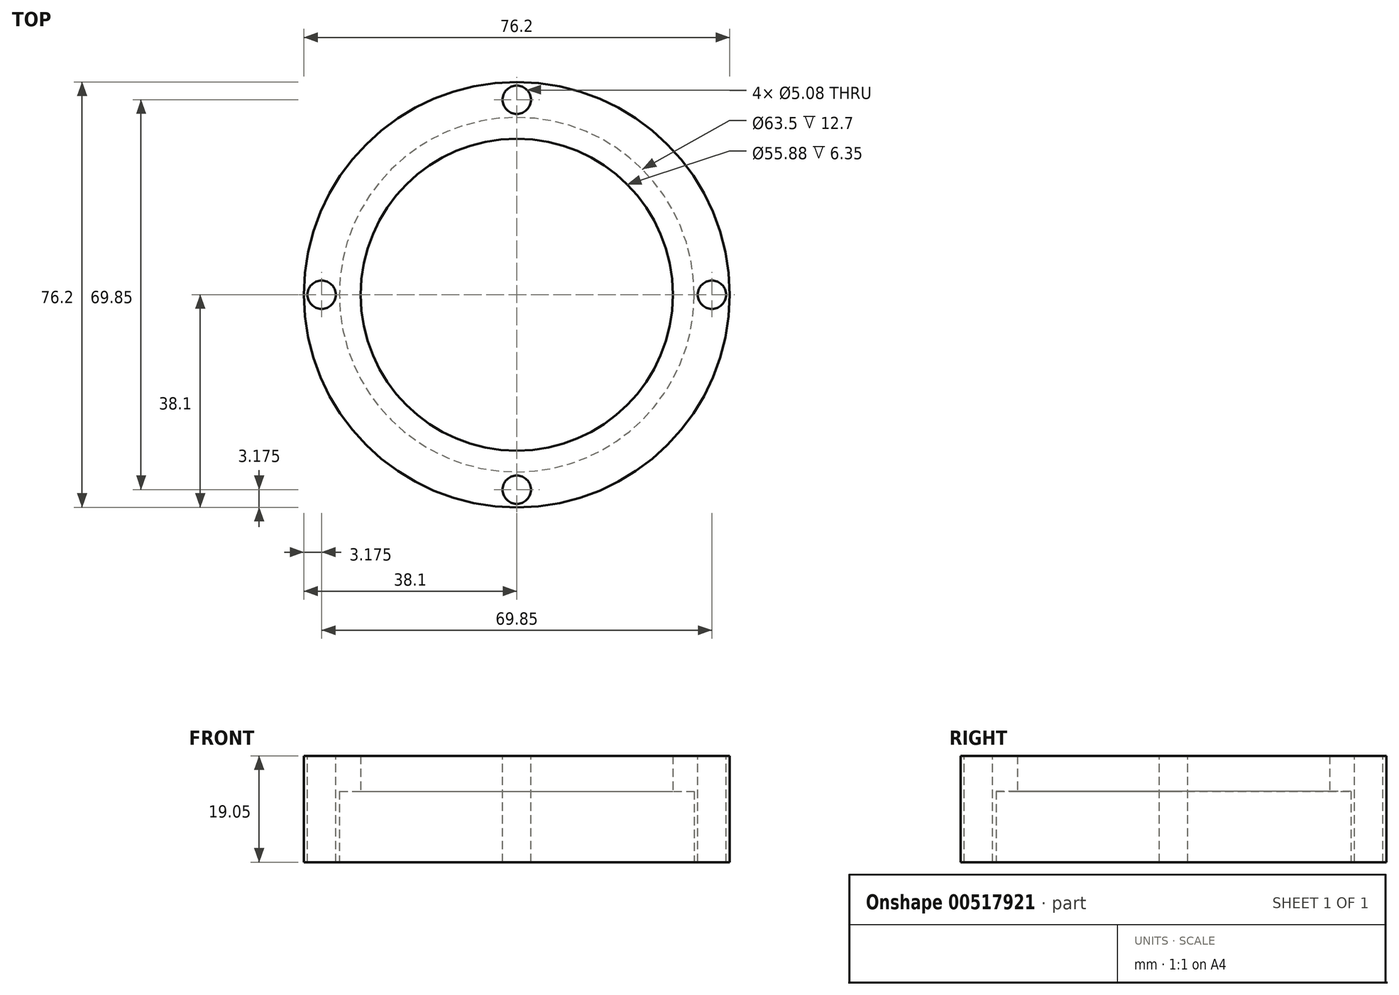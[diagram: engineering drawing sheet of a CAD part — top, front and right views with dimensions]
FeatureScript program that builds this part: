
annotation { "Feature Type Name" : "Feature", "Feature Type Description" : "" }
export const myFeature = defineFeature(function(context is Context, id is Id, definition is map)
    precondition{}
    {
        {
            var Q0;
            Q0=qCreatedBy(makeId("Right.planeOp"),FACE);
            var sketch = newSketch(context, id + "F0", { "sketchPlane" : qUnion([Q0])});
            skLineSegment(sketch, "E0", {"start": v(0, 0) * mm, "end": v(0, 27.2) * mm, "construction": true});
            skLineSegment(sketch, "E1", {"start": v(31.75, 0) * mm, "end": v(38.1, 0) * mm});
            skLineSegment(sketch, "E2", {"start": v(38.1, 0) * mm, "end": v(38.1, 19.05) * mm});
            skLineSegment(sketch, "E3", {"start": v(38.1, 19.05) * mm, "end": v(27.94, 19.05) * mm});
            skLineSegment(sketch, "E4", {"start": v(27.94, 19.05) * mm, "end": v(27.94, 12.7) * mm});
            skLineSegment(sketch, "E5", {"start": v(27.94, 12.7) * mm, "end": v(31.75, 12.7) * mm});
            skLineSegment(sketch, "E6", {"start": v(31.75, 12.7) * mm, "end": v(31.75, 0) * mm});
            skSolve(sketch);
        }
        {
            var Q0;
            Q0 = qSketchRegion(id + "F0", true);
            var Q1;
            Q1=sQuery(id+"F0.wireOp",EDGE,"E0");
            revolve(context, id + "F1", {"entities" : qUnion([Q0]), "axis" : qUnion([Q1]), "revolveType" : RevolveType.FULL});
        }
        {
            var Q0;
            Q0=makeQuery(id+"F1.opRevolve","SWEPT_FACE",FACE,{"disambiguationData":[OSD([sQuery(id+"F0.wireOp",EDGE,"E3")])]});
            var sketch = newSketch(context, id + "F2", { "sketchPlane" : qUnion([Q0])});
            skLineSegment(sketch, "E7", {"start": v(-53.02, 0) * mm, "end": v(61.8, 0) * mm, "construction": true});
            skLineSegment(sketch, "E8", {"start": v(0, -56.59) * mm, "end": v(0, 56.86) * mm, "construction": true});
            skCircle(sketch, "E9", {"center": v(0, 0) * mm, "radius": 34.93 * mm, "construction": true});
            skCircle(sketch, "E10", {"center": v(-34.93, 0) * mm, "radius": 2.54 * mm});
            skCircle(sketch, "E11", {"center": v(0, 34.93) * mm, "radius": 2.54 * mm});
            skCircle(sketch, "E12", {"center": v(34.93, 0) * mm, "radius": 2.54 * mm});
            skCircle(sketch, "E13", {"center": v(0, -34.93) * mm, "radius": 2.54 * mm});
            skSolve(sketch);
        }
        {
            var Q0;
            Q0 = qSketchRegion(id + "F2", true);
            extrude(context, id + "F3", {"entities" : qUnion([Q0]), "operationType" : NewBodyOperationType.REMOVE, "oppositeDirection" : true, "depth" : 25.4 * mm, "offsetDistance" : 25.4 * mm});
        }
    });
